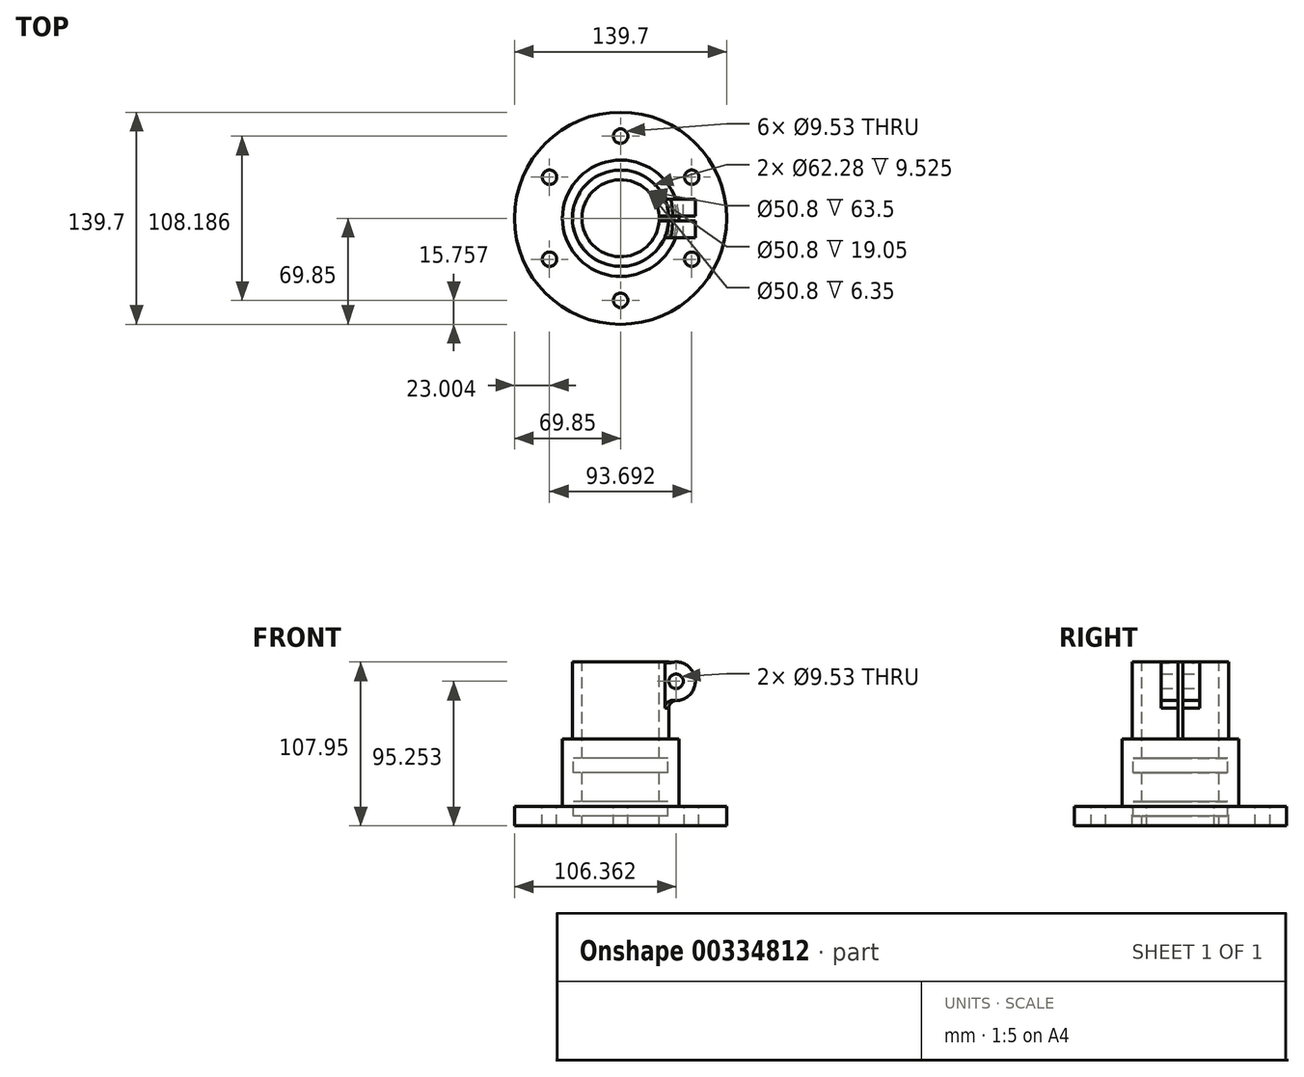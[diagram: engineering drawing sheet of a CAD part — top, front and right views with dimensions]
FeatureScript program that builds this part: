
annotation { "Feature Type Name" : "Feature", "Feature Type Description" : "" }
export const myFeature = defineFeature(function(context is Context, id is Id, definition is map)
    precondition{}
    {
        {
            var Q0;
            Q0=qCreatedBy(makeId("Front.planeOp"),FACE);
            var sketch = newSketch(context, id + "F0", { "sketchPlane" : qUnion([Q0])});
            skLineSegment(sketch, "E0", {"start": v(0, 329.77) * mm, "end": v(0, -319.17) * mm, "construction": true});
            skLineSegment(sketch, "E1", {"start": v(56.21, -220.24) * mm, "end": v(69.85, -220.24) * mm});
            skLineSegment(sketch, "E2", {"start": v(69.85, -220.24) * mm, "end": v(69.85, -207.54) * mm});
            skLineSegment(sketch, "E3", {"start": v(38.34, -163.09) * mm, "end": v(31.75, -163.09) * mm});
            skLineSegment(sketch, "E4", {"start": v(31.75, -163.09) * mm, "end": v(31.75, -112.29) * mm});
            skLineSegment(sketch, "E5", {"start": v(31.75, -112.29) * mm, "end": v(25.4, -112.29) * mm});
            skLineSegment(sketch, "E6", {"start": v(25.4, -112.29) * mm, "end": v(25.4, -175.79) * mm});
            skLineSegment(sketch, "E7", {"start": v(25.4, -175.79) * mm, "end": v(31.14, -175.79) * mm});
            skLineSegment(sketch, "E8", {"start": v(31.14, -175.79) * mm, "end": v(31.14, -185.31) * mm});
            skLineSegment(sketch, "E9", {"start": v(31.14, -185.31) * mm, "end": v(25.4, -185.31) * mm});
            skLineSegment(sketch, "E10", {"start": v(25.4, -185.31) * mm, "end": v(25.4, -204.36) * mm});
            skLineSegment(sketch, "E11", {"start": v(25.4, -204.36) * mm, "end": v(31.14, -204.36) * mm});
            skLineSegment(sketch, "E12", {"start": v(31.14, -204.36) * mm, "end": v(31.14, -213.89) * mm});
            skLineSegment(sketch, "E13", {"start": v(31.14, -213.89) * mm, "end": v(25.4, -213.89) * mm});
            skLineSegment(sketch, "E14", {"start": v(25.4, -213.89) * mm, "end": v(25.4, -220.24) * mm});
            skLineSegment(sketch, "E15", {"start": v(25.4, -220.24) * mm, "end": v(56.21, -220.24) * mm});
            skLineSegment(sketch, "E16", {"start": v(38.34, -163.09) * mm, "end": v(38.34, -207.54) * mm});
            skLineSegment(sketch, "E17", {"start": v(38.34, -207.54) * mm, "end": v(69.85, -207.54) * mm});
            skSolve(sketch);
        }
        {
            var Q0;
            Q0=makeQuery(id+"F0.imprint","IMPRINT",FACE,{"disambiguationData":[TD([[makeQuery(id+"F0.imprint","IMPRINT",EDGE,{"derivedFrom":sQuery(id+"F0.wireOp",EDGE,"E1")}),1.0]])]});
            var Q1;
            Q1=sQuery(id+"F0.wireOp",EDGE,"E0");
            revolve(context, id + "F1", {"entities" : qUnion([Q0]), "axis" : qUnion([Q1]), "revolveType" : RevolveType.FULL});
        }
        {
            var Q0;
            Q0=makeQuery(id+"F1.opRevolve","SWEPT_FACE",FACE,{"disambiguationData":[OSD([sQuery(id+"F0.wireOp",EDGE,"E17")])]});
            var sketch = newSketch(context, id + "F2", { "sketchPlane" : qUnion([Q0])});
            skLineSegment(sketch, "E18", {"start": v(0, 69.85) * mm, "end": v(0, 38.34) * mm, "construction": true});
            skCircle(sketch, "E19", {"center": v(0, 54.1) * mm, "radius": 4.76 * mm});
            skCircle(sketch, "E20.1.0", {"center": v(-46.85, 27.05) * mm, "radius": 4.76 * mm});
            skCircle(sketch, "E20.2.0", {"center": v(-46.85, -27.05) * mm, "radius": 4.76 * mm});
            skCircle(sketch, "E20.3.0", {"center": v(0, -54.1) * mm, "radius": 4.76 * mm});
            skCircle(sketch, "E20.4.0", {"center": v(46.85, -27.05) * mm, "radius": 4.76 * mm});
            skCircle(sketch, "E20.5.0", {"center": v(46.85, 27.05) * mm, "radius": 4.76 * mm});
            skPoint(sketch, "E20.center", {"position": v(0, 0) * mm});
            skSolve(sketch);
        }
        {
            var Q0;
            Q0 = qSketchRegion(id + "F2", true);
            extrude(context, id + "F3", {"entities" : qUnion([Q0]), "operationType" : NewBodyOperationType.REMOVE, "endBound" : BoundingType.THROUGH_ALL, "oppositeDirection" : true, "depth" : 25.4 * mm});
        }
        {
            var Q0;
            Q0=qCreatedBy(makeId("Front.planeOp"),FACE);
            var sketch = newSketch(context, id + "F4", { "sketchPlane" : qUnion([Q0])});
            skLineSegment(sketch, "E21", {"start": v(0, -170.37) * mm, "end": v(0, -83.63) * mm, "construction": true});
            skArc(sketch, "E22", {"start": v(25.4, -131.14) * mm, "mid": v(49.21, -124.99) * mm, "end": v(25.4, -118.84) * mm});
            skCircle(sketch, "E23", {"center": v(36.51, -124.99) * mm, "radius": 4.76 * mm});
            skLineSegment(sketch, "E24", {"start": v(31.75, -112.29) * mm, "end": v(31.75, -163.09) * mm, "construction": true});
            skLineSegment(sketch, "E25.0", {"start": v(-31.75, -112.29) * mm, "end": v(31.75, -112.29) * mm, "construction": true});
            skLineSegment(sketch, "E26.0", {"start": v(-38.34, -163.09) * mm, "end": v(38.34, -163.09) * mm, "construction": true});
            skLineSegment(sketch, "E27", {"start": v(25.4, -112.29) * mm, "end": v(25.4, -163.09) * mm, "construction": true});
            skLineSegment(sketch, "E28", {"start": v(25.4, -118.84) * mm, "end": v(25.4, -131.14) * mm});
            skSolve(sketch);
        }
        {
            var Q0;
            Q0 = qSketchRegion(id + "F4", true);
            extrude(context, id + "F5", {"entities" : qUnion([Q0]), "operationType" : NewBodyOperationType.ADD, "depth" : 25.4 * mm, "symmetric" : true});
        }
        {
            var Q0;
            Q0=makeQuery(id+"F1.opRevolve","SWEPT_FACE",FACE,{"disambiguationData":[OSD([sQuery(id+"F0.wireOp",EDGE,"E5")])]});
            var sketch = newSketch(context, id + "F6", { "sketchPlane" : qUnion([Q0])});
            skLineSegment(sketch, "E29", {"start": v(0, 0) * mm, "end": v(54.88, 0) * mm, "construction": true});
            skLineSegment(sketch, "E30.bottom", {"start": v(25.35, 1.59) * mm, "end": v(49.25, 1.59) * mm, "construction": true});
            skLineSegment(sketch, "E30.top", {"start": v(25.35, -1.59) * mm, "end": v(49.25, -1.59) * mm, "construction": true});
            skLineSegment(sketch, "E30.left", {"start": v(25.35, 1.59) * mm, "end": v(25.35, -1.59) * mm, "construction": true});
            skLineSegment(sketch, "E30.right", {"start": v(49.25, 1.59) * mm, "end": v(49.25, -1.59) * mm, "construction": true});
            skLineSegment(sketch, "E31", {"start": v(25.35, 1.59) * mm, "end": v(49.25, 1.59) * mm});
            skLineSegment(sketch, "E32", {"start": v(49.25, -1.59) * mm, "end": v(25.35, -1.59) * mm});
            skLineSegment(sketch, "E33", {"start": v(49.25, 1.59) * mm, "end": v(49.25, -1.59) * mm});
            skLineSegment(sketch, "E34", {"start": v(25.35, 1.59) * mm, "end": v(25.35, -1.59) * mm});
            skSolve(sketch);
        }
        {
            var Q0;
            Q0 = qSketchRegion(id + "F6", true);
            extrude(context, id + "F7", {"entities" : qUnion([Q0]), "operationType" : NewBodyOperationType.REMOVE, "oppositeDirection" : true, "depth" : 50.8 * mm});
        }
        {
            var Q0;
            {var subQ0=makeQuery(id+"F1.opRevolve","SWEPT_FACE",FACE,{"disambiguationData":[OSD([sQuery(id+"F0.wireOp",EDGE,"E4")])]});var subQ1=sQuery(id+"F4.wireOp",EDGE,"E22");var subQ2=makeQuery(id+"F5.opExtrude","SWEPT_FACE",FACE,{"disambiguationData":[OSD([subQ1])]});Q0=makeQuery(id+"F7.boolean.opBoolean","SPLIT",EDGE,{"disambiguationData":[TD([makeQuery(id+"F7.opExtrude","SWEPT_FACE",FACE,{"disambiguationData":[OSD([sQuery(id+"F6.wireOp",EDGE,"E31")])]})])],"derivedFrom":makeQuery(id+"F5.boolean.opBoolean","INTERSECT",EDGE,{"disambiguationData":[OD(0.0)],"derivedFrom":[subQ0,subQ2]})});}
            fillet(context, id + "F8", {"entities" : qUnion([Q0]), "radius" : 5.08 * mm, "tangentPropagation" : true, "allowEdgeOverflow" : false});
        }
        {
            var Q0;
            {var subQ0=makeQuery(id+"F1.opRevolve","SWEPT_FACE",FACE,{"disambiguationData":[OSD([sQuery(id+"F0.wireOp",EDGE,"E4")])]});var subQ1=sQuery(id+"F4.wireOp",EDGE,"E22");var subQ2=makeQuery(id+"F5.opExtrude","SWEPT_FACE",FACE,{"disambiguationData":[OSD([subQ1])]});Q0=makeQuery(id+"F7.boolean.opBoolean","SPLIT",EDGE,{"disambiguationData":[TD([makeQuery(id+"F7.opExtrude","SWEPT_FACE",FACE,{"disambiguationData":[OSD([sQuery(id+"F6.wireOp",EDGE,"E32")])]})])],"derivedFrom":makeQuery(id+"F5.boolean.opBoolean","INTERSECT",EDGE,{"disambiguationData":[OD(0.0)],"derivedFrom":[subQ0,subQ2]})});}
            fillet(context, id + "F9", {"entities" : qUnion([Q0]), "radius" : 5.08 * mm, "tangentPropagation" : true, "allowEdgeOverflow" : false});
        }
        {
            var Q0;
            {var subQ0=makeQuery(id+"F1.opRevolve","SWEPT_FACE",FACE,{"disambiguationData":[OSD([sQuery(id+"F0.wireOp",EDGE,"E4")])]});var subQ1=sQuery(id+"F4.wireOp",EDGE,"E22");var subQ2=makeQuery(id+"F5.opExtrude","SWEPT_FACE",FACE,{"disambiguationData":[OSD([subQ1])]});Q0=makeQuery(id+"F7.boolean.opBoolean","SPLIT",EDGE,{"disambiguationData":[TD([makeQuery(id+"F7.opExtrude","SWEPT_FACE",FACE,{"disambiguationData":[OSD([sQuery(id+"F6.wireOp",EDGE,"E32")])]})])],"derivedFrom":makeQuery(id+"F5.boolean.opBoolean","INTERSECT",EDGE,{"disambiguationData":[OD(1.0)],"derivedFrom":[subQ0,subQ2]})});}
            fillet(context, id + "F10", {"entities" : qUnion([Q0]), "radius" : 5.08 * mm, "tangentPropagation" : true, "allowEdgeOverflow" : false});
        }
        {
            var Q0;
            {var subQ0=makeQuery(id+"F1.opRevolve","SWEPT_FACE",FACE,{"disambiguationData":[OSD([sQuery(id+"F0.wireOp",EDGE,"E4")])]});var subQ1=sQuery(id+"F4.wireOp",EDGE,"E22");var subQ2=makeQuery(id+"F5.opExtrude","SWEPT_FACE",FACE,{"disambiguationData":[OSD([subQ1])]});Q0=makeQuery(id+"F7.boolean.opBoolean","SPLIT",EDGE,{"disambiguationData":[TD([makeQuery(id+"F7.opExtrude","SWEPT_FACE",FACE,{"disambiguationData":[OSD([sQuery(id+"F6.wireOp",EDGE,"E31")])]})])],"derivedFrom":makeQuery(id+"F5.boolean.opBoolean","INTERSECT",EDGE,{"disambiguationData":[OD(1.0)],"derivedFrom":[subQ0,subQ2]})});}
            fillet(context, id + "F11", {"entities" : qUnion([Q0]), "radius" : 5.08 * mm, "tangentPropagation" : true, "allowEdgeOverflow" : false});
        }
    });
